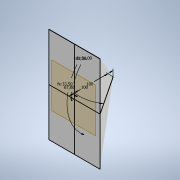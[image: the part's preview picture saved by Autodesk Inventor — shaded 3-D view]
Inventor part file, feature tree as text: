
AUTODESK INVENTOR PART (.ipt)
format: ipt  version: 2022 (Build 260153000, 153)  size: 120,320 bytes
history: native  units: mm
features: sketch x5, other x2, extrude x2, projected_geometry x1
ambient origin geometry x8: Origin, YZ Plane, XZ Plane, XY Plane, X Axis, Y Axis, Z Axis, Center Point
bodies: Body1 (feature_tree)
feature tree (10):
  other  "Твердое тело1"
  sketch  "Эскиз1"
  sketch  "Эскиз2"
  other  "РабПлоскость1"
  sketch  "Эскиз3"
  extrude  "Выдавливание1"  Depth=11.693706mm
  extrude  "Выдавливание2"  Depth=5.846853mm
  sketch  "Эскиз4"
  sketch  "Эскиз5"
  projected_geometry  "Спроецированная петля1"
